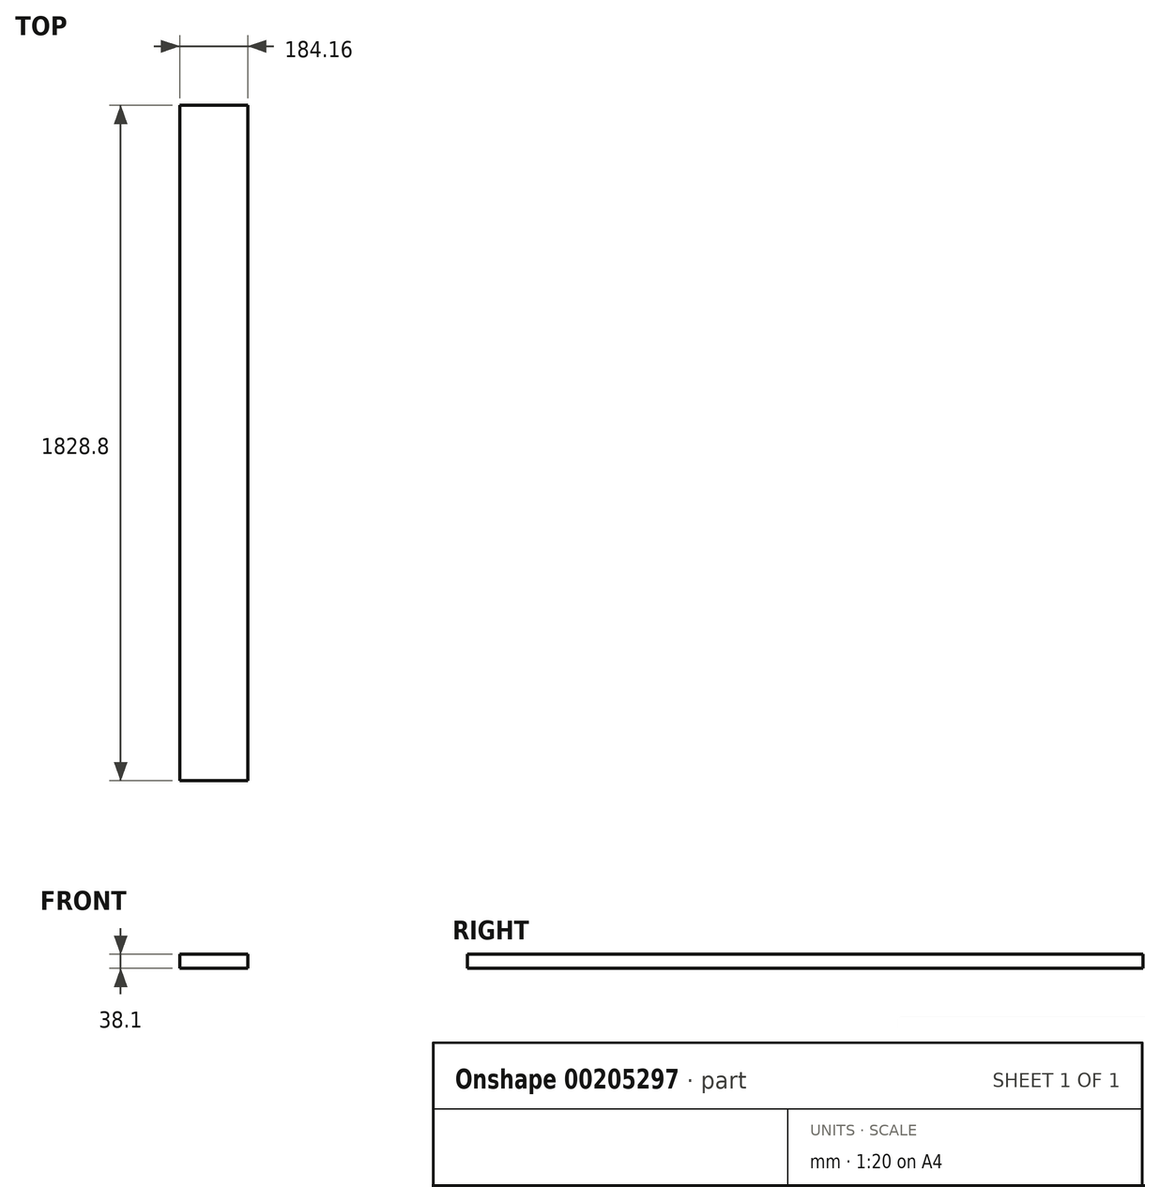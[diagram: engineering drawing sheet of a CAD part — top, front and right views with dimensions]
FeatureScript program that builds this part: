
annotation { "Feature Type Name" : "Feature", "Feature Type Description" : "" }
export const myFeature = defineFeature(function(context is Context, id is Id, definition is map)
    precondition{}
    {
        {
            var Q0;
            Q0=qCreatedBy(makeId("Front.planeOp"),FACE);
            var sketch = newSketch(context, id + "F0", { "sketchPlane" : qUnion([Q0])});
            skLineSegment(sketch, "E0.bottom", {"start": v(92.08, -19.05) * mm, "end": v(-92.08, -19.05) * mm});
            skLineSegment(sketch, "E0.top", {"start": v(92.08, 19.05) * mm, "end": v(-92.08, 19.05) * mm});
            skLineSegment(sketch, "E0.left", {"start": v(92.08, -19.05) * mm, "end": v(92.08, 19.05) * mm});
            skLineSegment(sketch, "E0.right", {"start": v(-92.08, -19.05) * mm, "end": v(-92.08, 19.05) * mm});
            skPoint(sketch, "E0.middle", {"position": v(0, 0) * mm});
            skSolve(sketch);
        }
        {
            var Q0;
            Q0=makeQuery(id+"F0.imprint","IMPRINT",FACE,{"disambiguationData":[TD([[makeQuery(id+"F0.imprint","IMPRINT",EDGE,{"derivedFrom":sQuery(id+"F0.wireOp",EDGE,"E0.bottom")}),-1.0]])]});
            extrude(context, id + "F1", {"entities" : qUnion([Q0]), "depth" : 914.4 * mm, "hasSecondDirection" : true, "secondDirectionOppositeDirection" : true, "secondDirectionDepth" : 914.4 * mm});
        }
        {
            var Q0;
            Q0=makeQuery(id+"F1.opExtrude","SWEPT_FACE",FACE,{"disambiguationData":[OSD([sQuery(id+"F0.wireOp",EDGE,"E0.bottom")])]});
            var sketch = newSketch(context, id + "F2", { "sketchPlane" : qUnion([Q0])});
            skCircle(sketch, "E1", {"center": v(41.28, 863.6) * mm, "radius": 44.45 * mm});
            skCircle(sketch, "E2", {"center": v(-41.28, 863.6) * mm, "radius": 44.45 * mm});
            skCircle(sketch, "E3", {"center": v(41.27, -863.6) * mm, "radius": 44.45 * mm});
            skCircle(sketch, "E4", {"center": v(-41.27, -863.6) * mm, "radius": 44.45 * mm});
            skSolve(sketch);
        }
        {
            var Q0;
            Q0=makeQuery(id+"F1.opExtrude","SWEPT_FACE",FACE,{"disambiguationData":[OSD([sQuery(id+"F0.wireOp",EDGE,"E0.top")])]});
            var sketch = newSketch(context, id + "F3", { "sketchPlane" : qUnion([Q0])});
            skCircle(sketch, "E5", {"center": v(0, -863.6) * mm, "radius": 38.1 * mm});
            skCircle(sketch, "E6", {"center": v(0, 0) * mm, "radius": 38.1 * mm});
            skCircle(sketch, "E7", {"center": v(0, 863.6) * mm, "radius": 38.1 * mm});
            skSolve(sketch);
        }
    });
